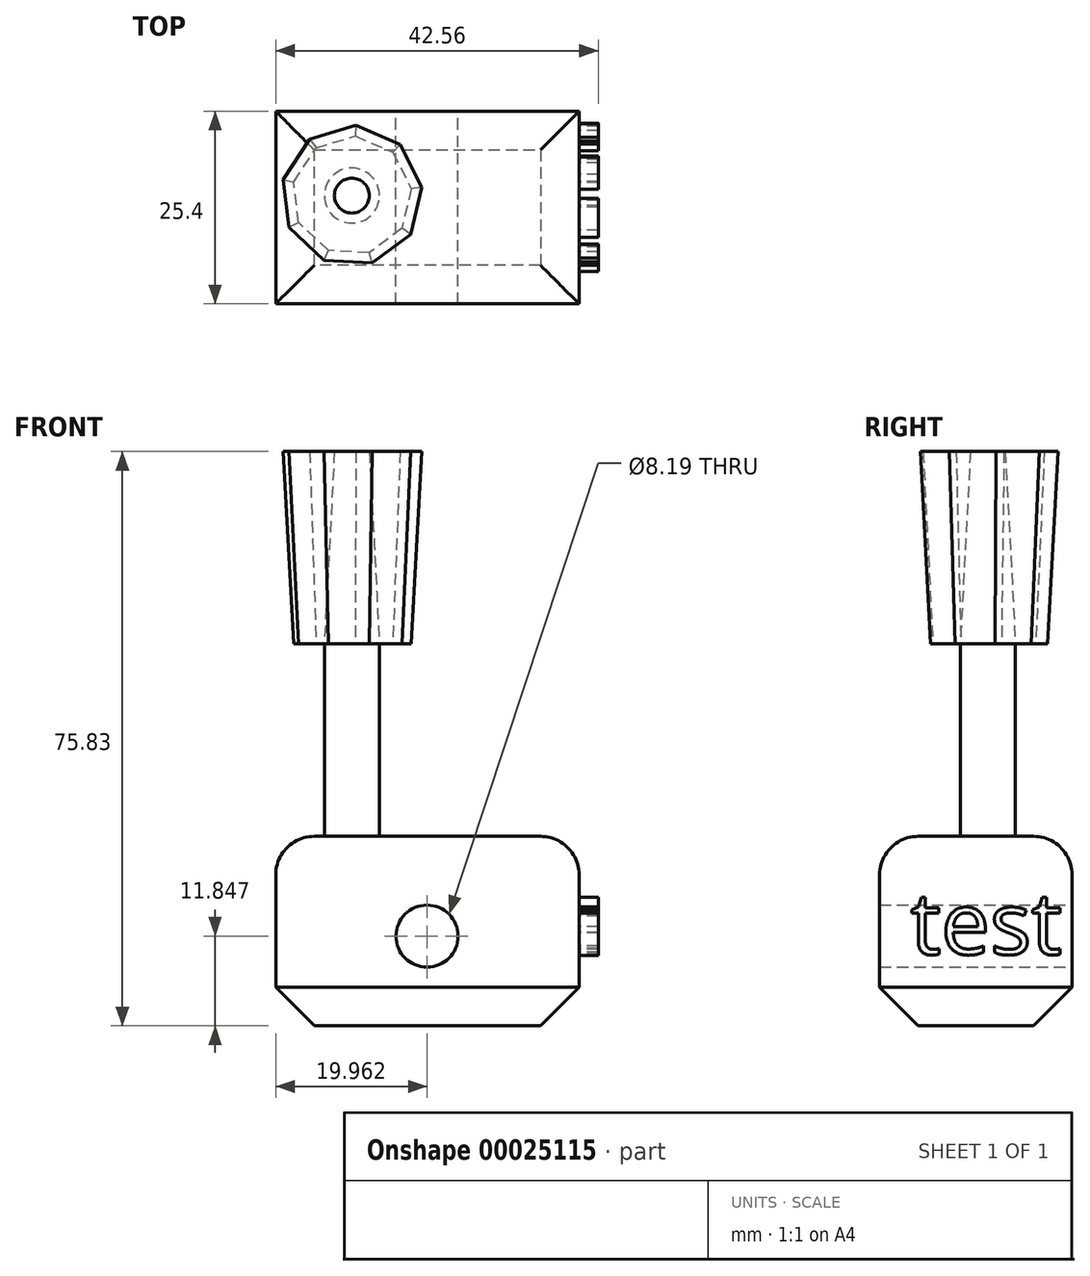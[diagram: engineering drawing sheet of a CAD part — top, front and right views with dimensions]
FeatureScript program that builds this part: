
annotation { "Feature Type Name" : "Feature", "Feature Type Description" : "" }
export const myFeature = defineFeature(function(context is Context, id is Id, definition is map)
    precondition{}
    {
        {
            var Q0;
            Q0=qCreatedBy(makeId("Front.planeOp"),FACE);
            var sketch = newSketch(context, id + "F0", { "sketchPlane" : qUnion([Q0])});
            skLineSegment(sketch, "E0.bottom", {"start": v(25.31, 39) * mm, "end": v(65.33, 39) * mm});
            skLineSegment(sketch, "E0.top", {"start": v(25.31, 64.02) * mm, "end": v(65.33, 64.02) * mm});
            skLineSegment(sketch, "E0.left", {"start": v(25.31, 39) * mm, "end": v(25.31, 64.02) * mm});
            skLineSegment(sketch, "E0.right", {"start": v(65.33, 39) * mm, "end": v(65.33, 64.02) * mm});
            skSolve(sketch);
        }
        {
            var Q0;
            Q0=makeQuery(id+"F0.imprint","IMPRINT",FACE,{"disambiguationData":[TD([[makeQuery(id+"F0.imprint","IMPRINT",EDGE,{"derivedFrom":sQuery(id+"F0.wireOp",EDGE,"E0.bottom")}),1.0]])]});
            extrude(context, id + "F1", {"entities" : qUnion([Q0]), "depth" : 25.4 * mm});
        }
        {
            var Q0;
            Q0 = qSketchRegion(id + "F0", true);
            extrude(context, id + "F2", {"entities" : qUnion([Q0]), "operationType" : NewBodyOperationType.ADD, "flatOperationType" : FlatOperationType.REMOVE, "offsetDistance" : 25.4 * mm, "depth" : 25.4 * mm, "domain" : OperationDomain.MODEL});
        }
        {
            var Q0;
            Q0=makeQuery(id+"F1.opExtrude","SWEPT_FACE",FACE,{"disambiguationData":[OSD([sQuery(id+"F0.wireOp",EDGE,"E0.top")])]});
            var sketch = newSketch(context, id + "F3", { "sketchPlane" : qUnion([Q0])});
            skSolve(sketch);
        }
        {
            var Q0;
            Q0=makeQuery(id+"F1.opExtrude","CAP_EDGE",EDGE,{"disambiguationData":[OSD([sQuery(id+"F0.wireOp",EDGE,"E0.top")])],"isStart":false});
            var Q1;
            Q1=makeQuery(id+"F1.opExtrude","SWEPT_EDGE",EDGE,{"disambiguationData":[OSD([sQuery(id+"F0.wireOp",EDGE,"E0.top"),sQuery(id+"F0.wireOp",EDGE,"E0.right")])]});
            var Q2;
            Q2=makeQuery(id+"F1.opExtrude","CAP_EDGE",EDGE,{"disambiguationData":[OSD([sQuery(id+"F0.wireOp",EDGE,"E0.top")])],"isStart":true});
            var Q3;
            Q3=makeQuery(id+"F1.opExtrude","SWEPT_EDGE",EDGE,{"disambiguationData":[OSD([sQuery(id+"F0.wireOp",EDGE,"E0.top"),sQuery(id+"F0.wireOp",EDGE,"E0.left")])]});
            fillet(context, id + "F4", {"entities" : qUnion([Q0, Q1, Q2, Q3]), "radius" : 5.08 * mm, "tangentPropagation" : true, "allowEdgeOverflow" : false});
        }
        {
            var Q0;
            Q0=makeQuery(id+"F1.opExtrude","SWEPT_EDGE",EDGE,{"disambiguationData":[OSD([sQuery(id+"F0.wireOp",EDGE,"E0.bottom"),sQuery(id+"F0.wireOp",EDGE,"E0.right")])]});
            var Q1;
            Q1=makeQuery(id+"F1.opExtrude","CAP_EDGE",EDGE,{"disambiguationData":[OSD([sQuery(id+"F0.wireOp",EDGE,"E0.bottom")])],"isStart":false});
            var Q2;
            Q2=makeQuery(id+"F1.opExtrude","SWEPT_EDGE",EDGE,{"disambiguationData":[OSD([sQuery(id+"F0.wireOp",EDGE,"E0.bottom"),sQuery(id+"F0.wireOp",EDGE,"E0.left")])]});
            var Q3;
            Q3=makeQuery(id+"F1.opExtrude","CAP_EDGE",EDGE,{"disambiguationData":[OSD([sQuery(id+"F0.wireOp",EDGE,"E0.bottom")])],"isStart":true});
            chamfer(context, id + "F5", {"entities" : qUnion([Q0, Q1, Q2, Q3]), "width" : 5.08 * mm, "tangentPropagation" : true});
        }
        {
            var Q0;
            Q0=makeQuery(id+"F0.imprint","IMPRINT",FACE,{"disambiguationData":[TD([[makeQuery(id+"F0.imprint","IMPRINT",EDGE,{"derivedFrom":sQuery(id+"F0.wireOp",EDGE,"E0.bottom")}),1.0]])]});
            var sketch = newSketch(context, id + "F6", { "sketchPlane" : qUnion([Q0])});
            skCircle(sketch, "E1", {"center": v(45.27, 50.84) * mm, "radius": 4.1 * mm});
            skSolve(sketch);
        }
        {
            var Q0;
            Q0 = qSketchRegion(id + "F6", true);
            var Q1;
            Q1=sQuery(id+"F6.wireOp",EDGE,"E1");
            extrude(context, id + "F7", {"entities" : qUnion([Q0]), "operationType" : NewBodyOperationType.REMOVE, "surfaceEntities" : qUnion([Q1]), "endBound" : BoundingType.THROUGH_ALL, "depth" : 25.4 * mm});
        }
        {
            var Q0;
            {var subQ0=sQuery(id+"F0.wireOp",EDGE,"E0.top");Q0=makeQuery(id+"F3.imprint","IMPRINT",FACE,{"disambiguationData":[TD([[makeQuery(id+"F3.imprint","IMPRINT",EDGE,{"derivedFrom":makeQuery(id+"F1.opExtrude","CAP_EDGE",EDGE,{"disambiguationData":[OSD([subQ0])],"isStart":true})}),-1.0]])]});}
            var sketch = newSketch(context, id + "F8", { "sketchPlane" : qUnion([Q0])});
            skCircle(sketch, "E2", {"center": v(53.4, -10.25) * mm, "radius": 2.68 * mm});
            skSolve(sketch);
        }
        {
            var Q0;
            Q0=makeQuery(id+"F8.imprint","IMPRINT",FACE,{"disambiguationData":[TD([[makeQuery(id+"F8.imprint","IMPRINT",EDGE,{"derivedFrom":sQuery(id+"F8.wireOp",EDGE,"E2")}),-1.0]])]});
            var sketch = newSketch(context, id + "F9", { "sketchPlane" : qUnion([Q0])});
            skCircle(sketch, "E3", {"center": v(35.35, -11.12) * mm, "radius": 3.63 * mm});
            skSolve(sketch);
        }
        {
            var Q0;
            Q0 = qSketchRegion(id + "F9", true);
            var Q1;
            Q1=sQuery(id+"F9.wireOp",EDGE,"E3");
            extrude(context, id + "F10", {"entities" : qUnion([Q0]), "surfaceEntities" : qUnion([Q1]), "depth" : 25.4 * mm});
        }
        {
            var Q0;
            Q0=makeQuery(id+"F10.opExtrude","CAP_FACE",FACE,{"disambiguationData":[OSD([sQuery(id+"F9.wireOp",EDGE,"E3")])],"isStart":false});
            var sketch = newSketch(context, id + "F11", { "sketchPlane" : qUnion([Q0])});
            skCircle(sketch, "E4.cCircle", {"center": v(35.35, -11.12) * mm, "radius": 7.4 * mm, "construction": true});
            skLineSegment(sketch, "E4.0", {"start": v(41.95, -15.44) * mm, "end": v(37.63, -18.67) * mm});
            skLineSegment(sketch, "E4.1", {"start": v(37.63, -18.67) * mm, "end": v(32.24, -18.36) * mm});
            skLineSegment(sketch, "E4.2", {"start": v(32.24, -18.36) * mm, "end": v(28.32, -14.67) * mm});
            skLineSegment(sketch, "E4.3", {"start": v(28.32, -14.67) * mm, "end": v(27.68, -9.31) * mm});
            skLineSegment(sketch, "E4.4", {"start": v(27.68, -9.31) * mm, "end": v(30.64, -4.8) * mm});
            skLineSegment(sketch, "E4.5", {"start": v(30.64, -4.8) * mm, "end": v(35.8, -3.25) * mm});
            skLineSegment(sketch, "E4.6", {"start": v(35.8, -3.25) * mm, "end": v(40.75, -5.38) * mm});
            skLineSegment(sketch, "E4.7", {"start": v(40.75, -5.38) * mm, "end": v(43.18, -10.2) * mm});
            skLineSegment(sketch, "E4.8", {"start": v(43.18, -10.2) * mm, "end": v(41.95, -15.44) * mm});
            skPoint(sketch, "E4.0.midPoint", {"position": v(39.79, -17.05) * mm});
            skSolve(sketch);
        }
        {
            var Q0;
            Q0=makeQuery(id+"F11.imprint","IMPRINT",FACE,{"disambiguationData":[TD([[makeQuery(id+"F11.imprint","IMPRINT",EDGE,{"derivedFrom":sQuery(id+"F11.wireOp",EDGE,"E4.0")}),-1.0]])]});
            extrude(context, id + "F12", {"entities" : qUnion([Q0]), "depth" : 25.4 * mm, "hasDraft" : true, "draftAngle" : 3 * degree});
        }
        {
            var Q0;
            Q0=makeQuery(id+"F1.opExtrude","SWEPT_FACE",FACE,{"disambiguationData":[OSD([sQuery(id+"F0.wireOp",EDGE,"E0.right")])]});
            var sketch = newSketch(context, id + "F13", { "sketchPlane" : qUnion([Q0])});
            skText(sketch, "E5", { "text": "test ", "fontName": "OpenSans-Regular.ttf"});
            const initialGuessF13  = {"E5": [-0.02134, 0.04843, 1, 0, 0.00826]};
            skSetInitialGuess(sketch, initialGuessF13);
            skSolve(sketch);
        }
        {
            var Q0;
            Q0 = qSketchRegion(id + "F13", true);
            extrude(context, id + "F14", {"entities" : qUnion([Q0]), "operationType" : NewBodyOperationType.ADD, "depth" : 2.54 * mm});
        }
    });
